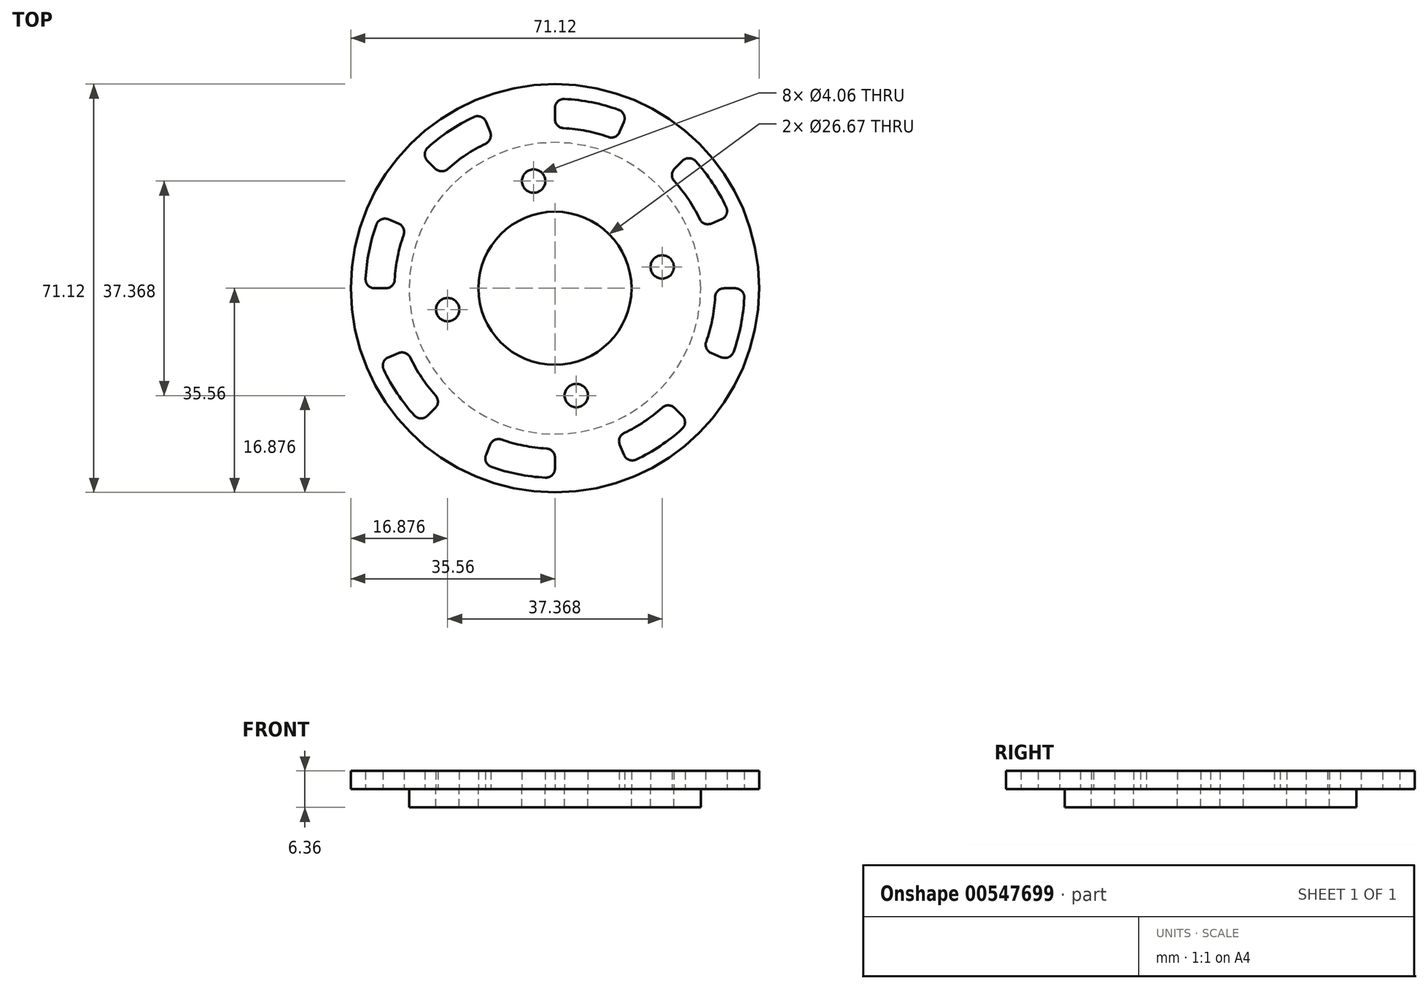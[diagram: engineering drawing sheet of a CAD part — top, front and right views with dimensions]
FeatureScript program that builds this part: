
annotation { "Feature Type Name" : "Feature", "Feature Type Description" : "" }
export const myFeature = defineFeature(function(context is Context, id is Id, definition is map)
    precondition{}
    {
        {
            var Q0;
            Q0=qCreatedBy(makeId("Top.planeOp"),FACE);
            var sketch = newSketch(context, id + "F0", { "sketchPlane" : qUnion([Q0])});
            skCircle(sketch, "E0", {"center": v(0, 0) * mm, "radius": 35.56 * mm});
            skCircle(sketch, "E1", {"center": v(0, 0) * mm, "radius": 33.02 * mm, "construction": true});
            skCircle(sketch, "E2", {"center": v(0, 0) * mm, "radius": 27.94 * mm, "construction": true});
            skLineSegment(sketch, "E3", {"start": v(0, 27.94) * mm, "end": v(0, 33.02) * mm});
            skLineSegment(sketch, "E4", {"start": v(10.7, 25.81) * mm, "end": v(12.64, 30.5) * mm});
            skArc(sketch, "E5", {"start": v(12.64, 30.5) * mm, "mid": v(6.44, 32.39) * mm, "end": v(0, 33.02) * mm});
            skArc(sketch, "E6", {"start": v(10.7, 25.81) * mm, "mid": v(5.45, 27.4) * mm, "end": v(0, 27.94) * mm});
            skLineSegment(sketch, "E7.1.0", {"start": v(-19.76, 19.76) * mm, "end": v(-23.35, 23.35) * mm});
            skLineSegment(sketch, "E7.1.1", {"start": v(-10.7, 25.81) * mm, "end": v(-12.64, 30.5) * mm});
            skArc(sketch, "E7.1.2", {"start": v(-12.64, 30.5) * mm, "mid": v(-18.34, 27.46) * mm, "end": v(-23.35, 23.35) * mm});
            skArc(sketch, "E7.1.3", {"start": v(-10.7, 25.81) * mm, "mid": v(-15.52, 23.23) * mm, "end": v(-19.76, 19.76) * mm});
            skLineSegment(sketch, "E7.2.0", {"start": v(-27.94, 0) * mm, "end": v(-33.02, 0) * mm});
            skLineSegment(sketch, "E7.2.1", {"start": v(-25.81, 10.7) * mm, "end": v(-30.5, 12.64) * mm});
            skArc(sketch, "E7.2.2", {"start": v(-30.5, 12.64) * mm, "mid": v(-32.39, 6.44) * mm, "end": v(-33.02, 0) * mm});
            skArc(sketch, "E7.2.3", {"start": v(-25.81, 10.7) * mm, "mid": v(-27.4, 5.45) * mm, "end": v(-27.94, 0) * mm});
            skLineSegment(sketch, "E7.3.0", {"start": v(-19.76, -19.76) * mm, "end": v(-23.35, -23.35) * mm});
            skLineSegment(sketch, "E7.3.1", {"start": v(-25.81, -10.7) * mm, "end": v(-30.5, -12.64) * mm});
            skArc(sketch, "E7.3.2", {"start": v(-30.5, -12.64) * mm, "mid": v(-27.46, -18.34) * mm, "end": v(-23.35, -23.35) * mm});
            skArc(sketch, "E7.3.3", {"start": v(-25.81, -10.7) * mm, "mid": v(-23.23, -15.52) * mm, "end": v(-19.76, -19.76) * mm});
            skCircle(sketch, "E8", {"center": v(0, 0) * mm, "radius": 13.34 * mm});
            skCircle(sketch, "E9", {"center": v(-3.72, 18.68) * mm, "radius": 2.03 * mm});
            skCircle(sketch, "E10", {"center": v(18.68, 3.72) * mm, "radius": 2.03 * mm});
            skCircle(sketch, "E11", {"center": v(-18.68, -3.72) * mm, "radius": 2.03 * mm});
            skCircle(sketch, "E12", {"center": v(3.72, -18.68) * mm, "radius": 2.03 * mm});
            skLineSegment(sketch, "E13", {"start": v(-3.72, 18.68) * mm, "end": v(3.72, -18.68) * mm, "construction": true});
            skLineSegment(sketch, "E14", {"start": v(-18.68, -3.72) * mm, "end": v(18.68, 3.72) * mm, "construction": true});
            skLineSegment(sketch, "E15", {"start": v(-10.7, 25.81) * mm, "end": v(0, 27.94) * mm, "construction": true});
            skCircle(sketch, "E16", {"center": v(0, 0) * mm, "radius": 25.4 * mm});
            skLineSegment(sketch, "E17.1.4.0", {"start": v(0, -27.94) * mm, "end": v(0, -33.02) * mm});
            skLineSegment(sketch, "E17.3.4.0", {"start": v(-10.7, -25.81) * mm, "end": v(-12.64, -30.5) * mm});
            skArc(sketch, "E17.6.4.0", {"start": v(-12.64, -30.5) * mm, "mid": v(-6.44, -32.39) * mm, "end": v(0, -33.02) * mm});
            skArc(sketch, "E17.10.4.0", {"start": v(-10.7, -25.81) * mm, "mid": v(-5.45, -27.4) * mm, "end": v(0, -27.94) * mm});
            skLineSegment(sketch, "E18.1.5.0", {"start": v(19.76, -19.76) * mm, "end": v(23.35, -23.35) * mm});
            skLineSegment(sketch, "E18.3.5.0", {"start": v(10.7, -25.81) * mm, "end": v(12.64, -30.5) * mm});
            skArc(sketch, "E18.6.5.0", {"start": v(12.64, -30.5) * mm, "mid": v(18.34, -27.46) * mm, "end": v(23.35, -23.35) * mm});
            skArc(sketch, "E18.10.5.0", {"start": v(10.7, -25.81) * mm, "mid": v(15.52, -23.23) * mm, "end": v(19.76, -19.76) * mm});
            skLineSegment(sketch, "E19.1.6.0", {"start": v(27.94, 0) * mm, "end": v(33.02, 0) * mm});
            skLineSegment(sketch, "E19.3.6.0", {"start": v(25.81, -10.7) * mm, "end": v(30.5, -12.64) * mm});
            skArc(sketch, "E19.6.6.0", {"start": v(30.5, -12.64) * mm, "mid": v(32.39, -6.44) * mm, "end": v(33.02, 0) * mm});
            skArc(sketch, "E19.10.6.0", {"start": v(25.81, -10.7) * mm, "mid": v(27.4, -5.45) * mm, "end": v(27.94, 0) * mm});
            skLineSegment(sketch, "E19.1.7.0", {"start": v(19.76, 19.76) * mm, "end": v(23.35, 23.35) * mm});
            skLineSegment(sketch, "E19.3.7.0", {"start": v(25.81, 10.7) * mm, "end": v(30.5, 12.64) * mm});
            skArc(sketch, "E19.6.7.0", {"start": v(30.5, 12.64) * mm, "mid": v(27.46, 18.34) * mm, "end": v(23.35, 23.35) * mm});
            skArc(sketch, "E19.10.7.0", {"start": v(25.81, 10.7) * mm, "mid": v(23.23, 15.52) * mm, "end": v(19.76, 19.76) * mm});
            skSolve(sketch);
        }
        {
            var Q0;
            Q0=makeQuery(id+"F0.imprint","IMPRINT",FACE,{"disambiguationData":[TD([[makeQuery(id+"F0.imprint","IMPRINT",EDGE,{"derivedFrom":sQuery(id+"F0.wireOp",EDGE,"E0")}),1.0]])]});
            var Q1;
            Q1=makeQuery(id+"F0.imprint","IMPRINT",FACE,{"disambiguationData":[TD([[makeQuery(id+"F0.imprint","IMPRINT",EDGE,{"derivedFrom":sQuery(id+"F0.wireOp",EDGE,"E8")}),-1.0]])]});
            extrude(context, id + "F1", {"entities" : qUnion([Q0, Q1]), "depth" : 3.17 * mm, "offsetDistance" : 25.4 * mm});
        }
        {
            var Q0;
            Q0=makeQuery(id+"F1.opExtrude","SWEPT_EDGE",EDGE,{"disambiguationData":[OSD([sQuery(id+"F0.wireOp",EDGE,"E7.1.1"),sQuery(id+"F0.wireOp",EDGE,"E7.1.2")])]});
            var Q1;
            Q1=makeQuery(id+"F1.opExtrude","SWEPT_EDGE",EDGE,{"disambiguationData":[OSD([sQuery(id+"F0.wireOp",EDGE,"E3"),sQuery(id+"F0.wireOp",EDGE,"E5")])]});
            var Q2;
            Q2=makeQuery(id+"F1.opExtrude","SWEPT_EDGE",EDGE,{"disambiguationData":[OSD([sQuery(id+"F0.wireOp",EDGE,"E7.3.0"),sQuery(id+"F0.wireOp",EDGE,"E7.3.3")])]});
            var Q3;
            Q3=makeQuery(id+"F1.opExtrude","SWEPT_EDGE",EDGE,{"disambiguationData":[OSD([sQuery(id+"F0.wireOp",EDGE,"E7.2.1"),sQuery(id+"F0.wireOp",EDGE,"E7.2.3")])]});
            var Q4;
            Q4=makeQuery(id+"F1.opExtrude","SWEPT_EDGE",EDGE,{"disambiguationData":[OSD([sQuery(id+"F0.wireOp",EDGE,"E7.1.0"),sQuery(id+"F0.wireOp",EDGE,"E7.1.2")])]});
            var Q5;
            Q5=makeQuery(id+"F1.opExtrude","SWEPT_EDGE",EDGE,{"disambiguationData":[OSD([sQuery(id+"F0.wireOp",EDGE,"E7.2.1"),sQuery(id+"F0.wireOp",EDGE,"E7.2.2")])]});
            var Q6;
            Q6=makeQuery(id+"F1.opExtrude","SWEPT_EDGE",EDGE,{"disambiguationData":[OSD([sQuery(id+"F0.wireOp",EDGE,"E7.3.1"),sQuery(id+"F0.wireOp",EDGE,"E7.3.3")])]});
            var Q7;
            Q7=makeQuery(id+"F1.opExtrude","SWEPT_EDGE",EDGE,{"disambiguationData":[OSD([sQuery(id+"F0.wireOp",EDGE,"E3"),sQuery(id+"F0.wireOp",EDGE,"E6")])]});
            var Q8;
            Q8=makeQuery(id+"F1.opExtrude","SWEPT_EDGE",EDGE,{"disambiguationData":[OSD([sQuery(id+"F0.wireOp",EDGE,"E4"),sQuery(id+"F0.wireOp",EDGE,"E6")])]});
            var Q9;
            Q9=makeQuery(id+"F1.opExtrude","SWEPT_EDGE",EDGE,{"disambiguationData":[OSD([sQuery(id+"F0.wireOp",EDGE,"E7.3.1"),sQuery(id+"F0.wireOp",EDGE,"E7.3.2")])]});
            var Q10;
            Q10=makeQuery(id+"F1.opExtrude","SWEPT_EDGE",EDGE,{"disambiguationData":[OSD([sQuery(id+"F0.wireOp",EDGE,"E7.2.0"),sQuery(id+"F0.wireOp",EDGE,"E7.2.2")])]});
            var Q11;
            Q11=makeQuery(id+"F1.opExtrude","SWEPT_EDGE",EDGE,{"disambiguationData":[OSD([sQuery(id+"F0.wireOp",EDGE,"E7.1.0"),sQuery(id+"F0.wireOp",EDGE,"E7.1.3")])]});
            var Q12;
            Q12=makeQuery(id+"F1.opExtrude","SWEPT_EDGE",EDGE,{"disambiguationData":[OSD([sQuery(id+"F0.wireOp",EDGE,"E4"),sQuery(id+"F0.wireOp",EDGE,"E5")])]});
            var Q13;
            Q13=makeQuery(id+"F1.opExtrude","SWEPT_EDGE",EDGE,{"disambiguationData":[OSD([sQuery(id+"F0.wireOp",EDGE,"E7.3.0"),sQuery(id+"F0.wireOp",EDGE,"E7.3.2")])]});
            var Q14;
            Q14=makeQuery(id+"F1.opExtrude","SWEPT_EDGE",EDGE,{"disambiguationData":[OSD([sQuery(id+"F0.wireOp",EDGE,"E7.2.0"),sQuery(id+"F0.wireOp",EDGE,"E7.2.3")])]});
            var Q15;
            Q15=makeQuery(id+"F1.opExtrude","SWEPT_EDGE",EDGE,{"disambiguationData":[OSD([sQuery(id+"F0.wireOp",EDGE,"E7.1.1"),sQuery(id+"F0.wireOp",EDGE,"E7.1.3")])]});
            var Q16;
            Q16=makeQuery(id+"F1.opExtrude","SWEPT_EDGE",EDGE,{"disambiguationData":[OSD([sQuery(id+"F0.wireOp",EDGE,"aa6108f5-4004-4f74-9787-b08779f10825.1.5.0"),sQuery(id+"F0.wireOp",EDGE,"aa6108f5-4004-4f74-9787-b08779f10825.6.5.0")])]});
            var Q17;
            Q17=makeQuery(id+"F1.opExtrude","SWEPT_EDGE",EDGE,{"disambiguationData":[OSD([sQuery(id+"F0.wireOp",EDGE,"aa6108f5-4004-4f74-9787-b08779f10825.1.5.0"),sQuery(id+"F0.wireOp",EDGE,"aa6108f5-4004-4f74-9787-b08779f10825.10.5.0")])]});
            var Q18;
            Q18=makeQuery(id+"F1.opExtrude","SWEPT_EDGE",EDGE,{"disambiguationData":[OSD([sQuery(id+"F0.wireOp",EDGE,"aa6108f5-4004-4f74-9787-b08779f10825.3.5.0"),sQuery(id+"F0.wireOp",EDGE,"aa6108f5-4004-4f74-9787-b08779f10825.10.5.0")])]});
            var Q19;
            Q19=makeQuery(id+"F1.opExtrude","SWEPT_EDGE",EDGE,{"disambiguationData":[OSD([sQuery(id+"F0.wireOp",EDGE,"aa6108f5-4004-4f74-9787-b08779f10825.3.5.0"),sQuery(id+"F0.wireOp",EDGE,"aa6108f5-4004-4f74-9787-b08779f10825.6.5.0")])]});
            var Q20;
            Q20=makeQuery(id+"F1.opExtrude","SWEPT_EDGE",EDGE,{"disambiguationData":[OSD([sQuery(id+"F0.wireOp",EDGE,"0f3900c4-58a8-429b-b535-d8ec087a8218.3.4.0"),sQuery(id+"F0.wireOp",EDGE,"0f3900c4-58a8-429b-b535-d8ec087a8218.6.4.0")])]});
            var Q21;
            Q21=makeQuery(id+"F1.opExtrude","SWEPT_EDGE",EDGE,{"disambiguationData":[OSD([sQuery(id+"F0.wireOp",EDGE,"0f3900c4-58a8-429b-b535-d8ec087a8218.3.4.0"),sQuery(id+"F0.wireOp",EDGE,"0f3900c4-58a8-429b-b535-d8ec087a8218.10.4.0")])]});
            var Q22;
            Q22=makeQuery(id+"F1.opExtrude","SWEPT_EDGE",EDGE,{"disambiguationData":[OSD([sQuery(id+"F0.wireOp",EDGE,"0f3900c4-58a8-429b-b535-d8ec087a8218.1.4.0"),sQuery(id+"F0.wireOp",EDGE,"0f3900c4-58a8-429b-b535-d8ec087a8218.10.4.0")])]});
            var Q23;
            Q23=makeQuery(id+"F1.opExtrude","SWEPT_EDGE",EDGE,{"disambiguationData":[OSD([sQuery(id+"F0.wireOp",EDGE,"0f3900c4-58a8-429b-b535-d8ec087a8218.1.4.0"),sQuery(id+"F0.wireOp",EDGE,"0f3900c4-58a8-429b-b535-d8ec087a8218.6.4.0")])]});
            var Q24;
            Q24=makeQuery(id+"F1.opExtrude","SWEPT_EDGE",EDGE,{"disambiguationData":[OSD([sQuery(id+"F0.wireOp",EDGE,"E19.1.7.0"),sQuery(id+"F0.wireOp",EDGE,"E19.6.7.0")])]});
            var Q25;
            Q25=makeQuery(id+"F1.opExtrude","SWEPT_EDGE",EDGE,{"disambiguationData":[OSD([sQuery(id+"F0.wireOp",EDGE,"E19.1.6.0"),sQuery(id+"F0.wireOp",EDGE,"E19.10.6.0")])]});
            var Q26;
            Q26=makeQuery(id+"F1.opExtrude","SWEPT_EDGE",EDGE,{"disambiguationData":[OSD([sQuery(id+"F0.wireOp",EDGE,"E18.1.5.0"),sQuery(id+"F0.wireOp",EDGE,"E18.10.5.0")])]});
            var Q27;
            Q27=makeQuery(id+"F1.opExtrude","SWEPT_EDGE",EDGE,{"disambiguationData":[OSD([sQuery(id+"F0.wireOp",EDGE,"E17.3.4.0"),sQuery(id+"F0.wireOp",EDGE,"E17.10.4.0")])]});
            var Q28;
            Q28=makeQuery(id+"F1.opExtrude","SWEPT_EDGE",EDGE,{"disambiguationData":[OSD([sQuery(id+"F0.wireOp",EDGE,"E19.1.7.0"),sQuery(id+"F0.wireOp",EDGE,"E19.10.7.0")])]});
            var Q29;
            Q29=makeQuery(id+"F1.opExtrude","SWEPT_EDGE",EDGE,{"disambiguationData":[OSD([sQuery(id+"F0.wireOp",EDGE,"E19.3.6.0"),sQuery(id+"F0.wireOp",EDGE,"E19.10.6.0")])]});
            var Q30;
            Q30=makeQuery(id+"F1.opExtrude","SWEPT_EDGE",EDGE,{"disambiguationData":[OSD([sQuery(id+"F0.wireOp",EDGE,"E18.3.5.0"),sQuery(id+"F0.wireOp",EDGE,"E18.10.5.0")])]});
            var Q31;
            Q31=makeQuery(id+"F1.opExtrude","SWEPT_EDGE",EDGE,{"disambiguationData":[OSD([sQuery(id+"F0.wireOp",EDGE,"E17.3.4.0"),sQuery(id+"F0.wireOp",EDGE,"E17.6.4.0")])]});
            var Q32;
            Q32=makeQuery(id+"F1.opExtrude","SWEPT_EDGE",EDGE,{"disambiguationData":[OSD([sQuery(id+"F0.wireOp",EDGE,"E19.3.7.0"),sQuery(id+"F0.wireOp",EDGE,"E19.10.7.0")])]});
            var Q33;
            Q33=makeQuery(id+"F1.opExtrude","SWEPT_EDGE",EDGE,{"disambiguationData":[OSD([sQuery(id+"F0.wireOp",EDGE,"E19.3.6.0"),sQuery(id+"F0.wireOp",EDGE,"E19.6.6.0")])]});
            var Q34;
            Q34=makeQuery(id+"F1.opExtrude","SWEPT_EDGE",EDGE,{"disambiguationData":[OSD([sQuery(id+"F0.wireOp",EDGE,"E18.3.5.0"),sQuery(id+"F0.wireOp",EDGE,"E18.6.5.0")])]});
            var Q35;
            Q35=makeQuery(id+"F1.opExtrude","SWEPT_EDGE",EDGE,{"disambiguationData":[OSD([sQuery(id+"F0.wireOp",EDGE,"E19.3.7.0"),sQuery(id+"F0.wireOp",EDGE,"E19.6.7.0")])]});
            var Q36;
            Q36=makeQuery(id+"F1.opExtrude","SWEPT_EDGE",EDGE,{"disambiguationData":[OSD([sQuery(id+"F0.wireOp",EDGE,"E18.1.5.0"),sQuery(id+"F0.wireOp",EDGE,"E18.6.5.0")])]});
            var Q37;
            Q37=makeQuery(id+"F1.opExtrude","SWEPT_EDGE",EDGE,{"disambiguationData":[OSD([sQuery(id+"F0.wireOp",EDGE,"E19.1.6.0"),sQuery(id+"F0.wireOp",EDGE,"E19.6.6.0")])]});
            var Q38;
            Q38=makeQuery(id+"F1.opExtrude","SWEPT_EDGE",EDGE,{"disambiguationData":[OSD([sQuery(id+"F0.wireOp",EDGE,"E17.1.4.0"),sQuery(id+"F0.wireOp",EDGE,"E17.10.4.0")])]});
            var Q39;
            Q39=makeQuery(id+"F1.opExtrude","SWEPT_EDGE",EDGE,{"disambiguationData":[OSD([sQuery(id+"F0.wireOp",EDGE,"E17.1.4.0"),sQuery(id+"F0.wireOp",EDGE,"E17.6.4.0")])]});
            fillet(context, id + "F2", {"entities" : qUnion([Q0, Q1, Q2, Q3, Q4, Q5, Q6, Q7, Q8, Q9, Q10, Q11, Q12, Q13, Q14, Q15, Q16, Q17, Q18, Q19, Q20, Q21, Q22, Q23, Q24, Q25, Q26, Q27, Q28, Q29, Q30, Q31, Q32, Q33, Q34, Q35, Q36, Q37, Q38, Q39]), "radius" : 1.59 * mm, "tangentPropagation" : true, "allowEdgeOverflow" : false});
        }
        {
            var Q0;
            Q0=makeQuery(id+"F0.imprint","IMPRINT",FACE,{"disambiguationData":[TD([[makeQuery(id+"F0.imprint","IMPRINT",EDGE,{"derivedFrom":sQuery(id+"F0.wireOp",EDGE,"E8")}),-1.0]])]});
            extrude(context, id + "F3", {"entities" : qUnion([Q0]), "oppositeDirection" : true, "depth" : 3.17 * mm, "offsetDistance" : 25.4 * mm});
        }
    });
